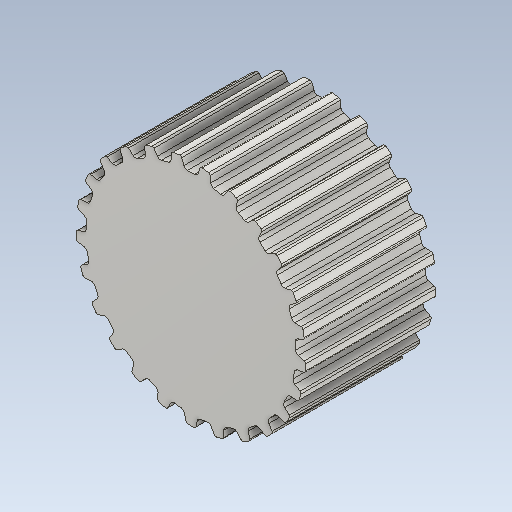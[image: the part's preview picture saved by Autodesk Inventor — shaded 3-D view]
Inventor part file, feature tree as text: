
AUTODESK INVENTOR PART (.ipt)
format: ipt  version: 2020 (Build 240168000, 168)  size: 373,248 bytes
history: native  units: mm (DEFAULTED — no unit token found)
features: other x3, extrude x2, fillet x1, pattern_circular x1
ambient origin geometry x8: Origin, YZ Plane, XZ Plane, XY Plane, X Axis, Y Axis, Z Axis, Center Point
bodies: Solid1 (feature_tree)
feature tree (7):
  other  "Pulley Sketch"
  extrude  "Base Body"  Depth=16.170142mm
  extrude  "Tooth"  Depth=0.254mm
  fillet  "Tooth Fillet"  Radius=0.6858mm
  pattern_circular  "Teeth"  [2 undecoded]
  other  "Left flange"
  other  "Right flange"
note: 2 required parameter values undecoded (feature->parameter linkage not recoverable at this tier; creation-order binding heuristic only, values carry confidence <= 0.55)
